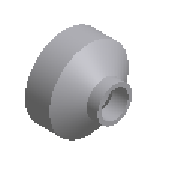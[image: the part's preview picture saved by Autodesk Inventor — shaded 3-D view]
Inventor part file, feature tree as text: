
AUTODESK INVENTOR PART (.ipt)
format: ipt  version: 2025 (Build 290162010, 162A)  size: 169,472 bytes
history: native  units: mm (DEFAULTED — no unit token found)
features: other x4, revolve x1
ambient origin geometry x8: Origin, YZ Plane, XZ Plane, XY Plane, X Axis, Y Axis, Z Axis, Center Point
bodies: Solid1 (feature_tree)
feature tree (5):
  revolve  "Revolution1"  [1 undecoded]
  other  "Work Axis1"
  other  "Work Point1"
  other  "Work Axis2"
  other  "Work Point2"
note: 1 required parameter value undecoded (feature->parameter linkage not recoverable at this tier; creation-order binding heuristic only, values carry confidence <= 0.55)
